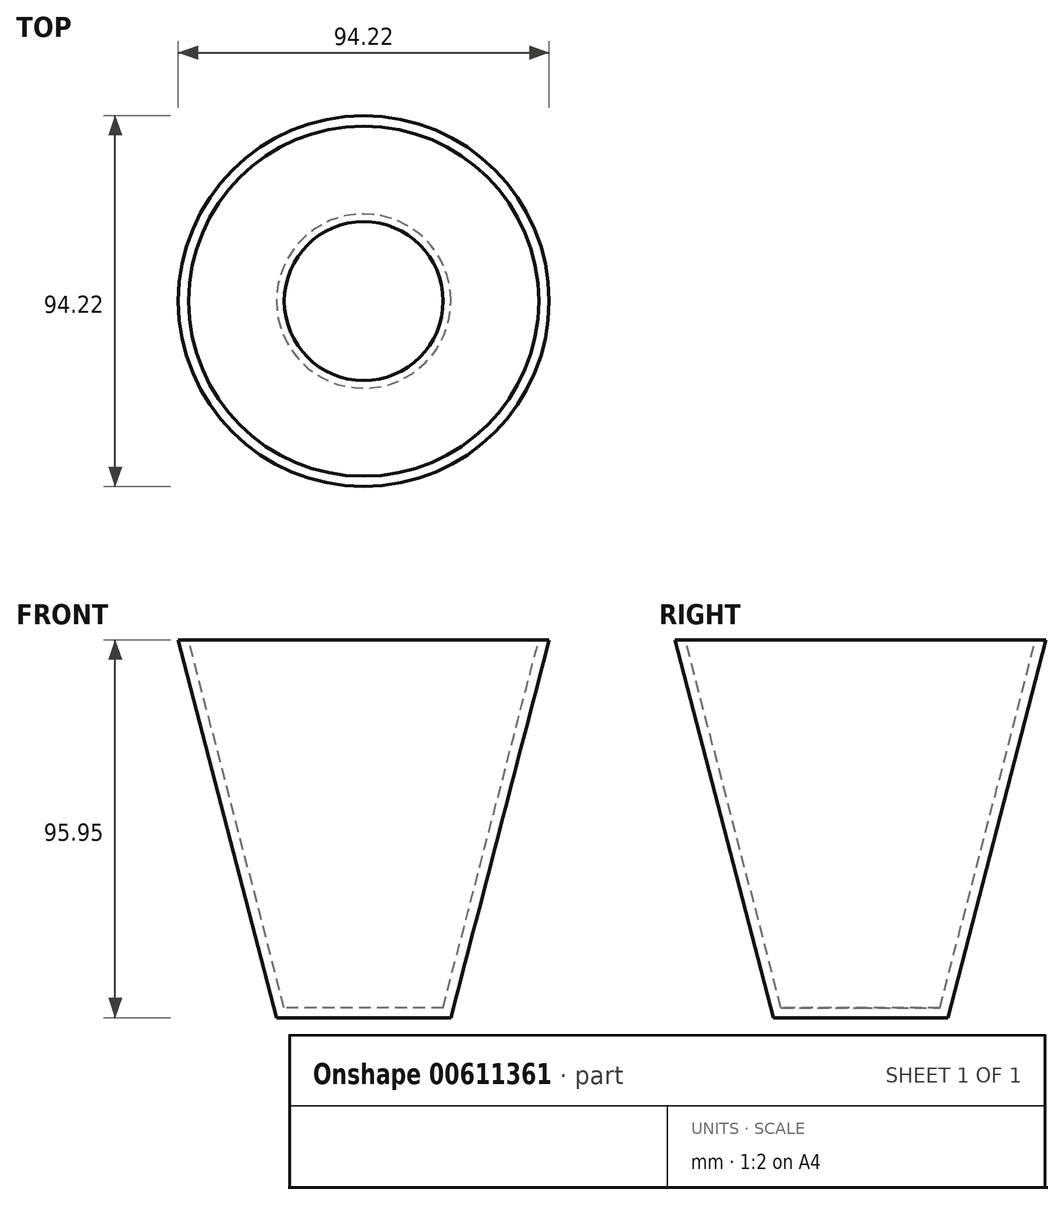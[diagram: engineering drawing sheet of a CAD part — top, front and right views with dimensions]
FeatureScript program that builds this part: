
annotation { "Feature Type Name" : "Feature", "Feature Type Description" : "" }
export const myFeature = defineFeature(function(context is Context, id is Id, definition is map)
    precondition{}
    {
        {
            var Q0;
            Q0=qCreatedBy(makeId("Front.planeOp"),FACE);
            var sketch = newSketch(context, id + "F0", { "sketchPlane" : qUnion([Q0])});
            skLineSegment(sketch, "E0", {"start": v(0, 50.68) * mm, "end": v(0, -45.27) * mm});
            skLineSegment(sketch, "E1", {"start": v(0, -45.27) * mm, "end": v(-22.14, -45.27) * mm});
            skLineSegment(sketch, "E2", {"start": v(-22.14, -45.27) * mm, "end": v(-47.1, 50.68) * mm});
            skLineSegment(sketch, "E3", {"start": v(-47.1, 50.68) * mm, "end": v(0, 50.68) * mm});
            skLineSegment(sketch, "E4", {"start": v(0, 66.93) * mm, "end": v(0, -70.58) * mm, "construction": true});
            skSolve(sketch);
        }
        {
            var Q0;
            Q0=makeQuery(id+"F0.imprint","IMPRINT",FACE,{"disambiguationData":[TD([[makeQuery(id+"F0.imprint","IMPRINT",EDGE,{"derivedFrom":sQuery(id+"F0.wireOp",EDGE,"E0")}),-1.0]])]});
            var Q1;
            Q1 = qConstructionFilter(qBodyType(qCreatedBy(id + "F0" ,EDGE), BodyType.WIRE), ConstructionObject.NO);
            var Q2;
            Q2=sQuery(id+"F0.wireOp",EDGE,"E4");
            revolve(context, id + "F1", {"entities" : qUnion([Q0]), "surfaceEntities" : qUnion([Q1]), "axis" : qUnion([Q2]), "revolveType" : RevolveType.FULL});
        }
        {
            var Q0;
            Q0=makeQuery(id+"F1.opRevolve","SWEPT_FACE",FACE,{"disambiguationData":[OSD([sQuery(id+"F0.wireOp",EDGE,"E3")])]});
            shell(context, id + "F2", {"entities" : qUnion([Q0]), "thickness" : 2.54 * mm});
        }
    });
